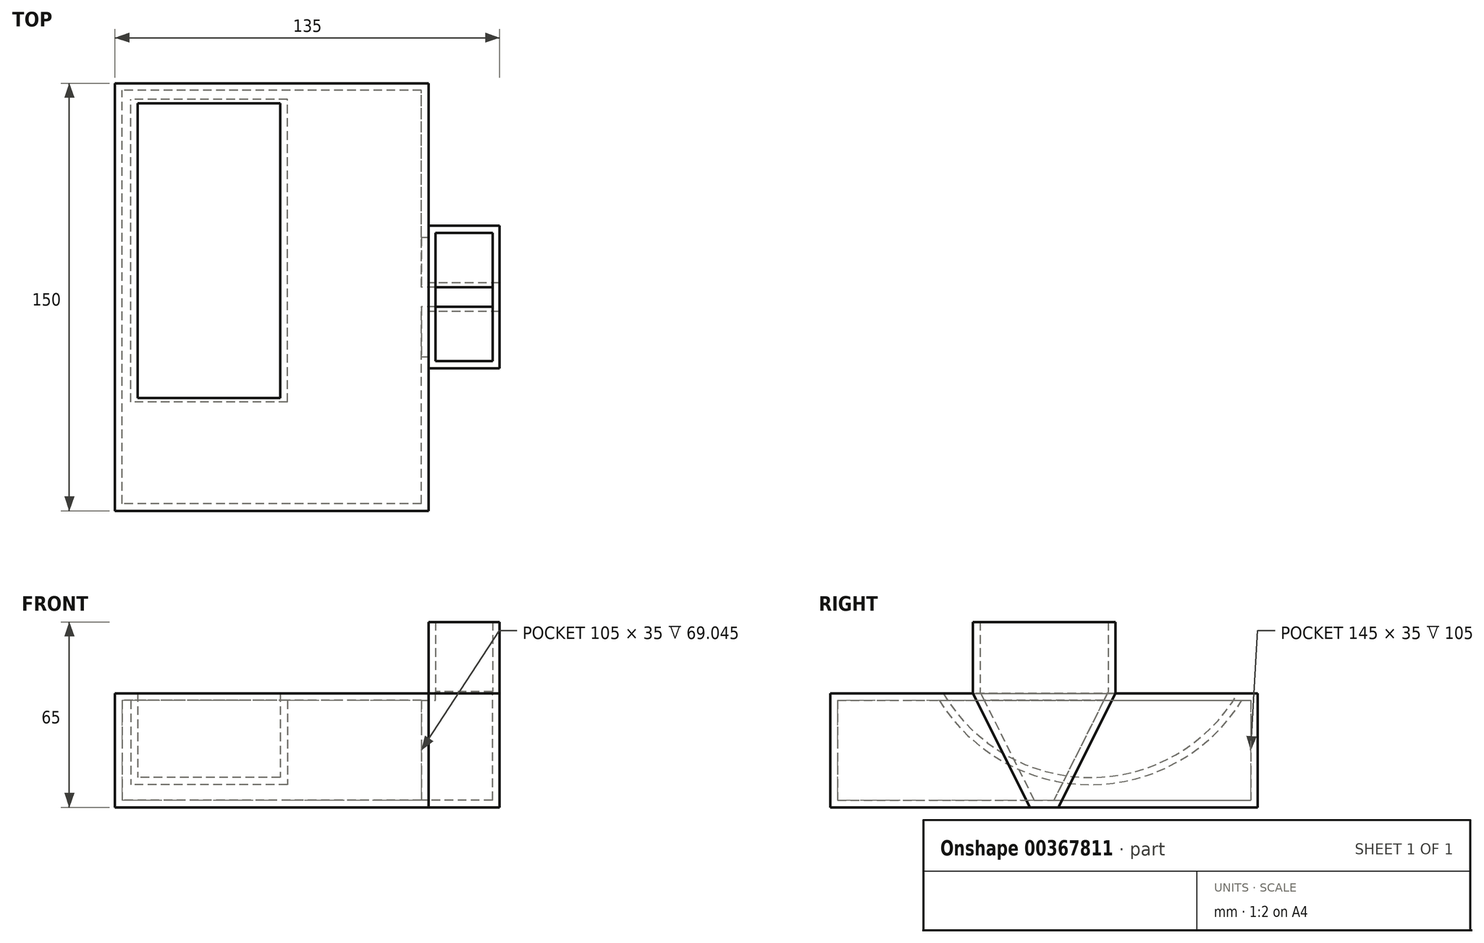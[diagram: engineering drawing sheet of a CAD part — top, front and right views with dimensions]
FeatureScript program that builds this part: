
annotation { "Feature Type Name" : "Feature", "Feature Type Description" : "" }
export const myFeature = defineFeature(function(context is Context, id is Id, definition is map)
    precondition{}
    {
        {
            var Q0;
            Q0=qCreatedBy(makeId("Top.planeOp"),FACE);
            var sketch = newSketch(context, id + "F0", { "sketchPlane" : qUnion([Q0])});
            skLineSegment(sketch, "E0.bottom", {"start": v(55, -75) * mm, "end": v(-55, -75) * mm});
            skLineSegment(sketch, "E0.top", {"start": v(55, 75) * mm, "end": v(-55, 75) * mm});
            skLineSegment(sketch, "E0.left", {"start": v(55, -75) * mm, "end": v(55, 75) * mm});
            skLineSegment(sketch, "E0.right", {"start": v(-55, -75) * mm, "end": v(-55, 75) * mm});
            skPoint(sketch, "E0.middle", {"position": v(0, 0) * mm});
            skSolve(sketch);
        }
        {
            var Q0;
            Q0=makeQuery(id+"F0.imprint","IMPRINT",FACE,{"disambiguationData":[TD([[makeQuery(id+"F0.imprint","IMPRINT",EDGE,{"derivedFrom":sQuery(id+"F0.wireOp",EDGE,"E0.bottom")}),-1.0]])]});
            extrude(context, id + "F1", {"entities" : qUnion([Q0]), "depth" : 40 * mm});
        }
        {
            var Q0;
            Q0=qCreatedBy(makeId("Right.planeOp"),FACE);
            cPlane(context, id + "F2", {"entities" : qUnion([Q0]), "cplaneType" : CPlaneType.OFFSET, "offset" : 47 * mm, "oppositeDirection" : true, "width" : 150 * mm, "height" : 150 * mm});
        }
        {
            var Q0;
            Q0=qCreatedBy(id+"F2.planeOp",FACE);
            var sketch = newSketch(context, id + "F3", { "sketchPlane" : qUnion([Q0])});
            skCircle(sketch, "E1", {"center": v(16.3, 70.46) * mm, "radius": 60 * mm});
            skSolve(sketch);
        }
        {
            var Q0;
            Q0=makeQuery(id+"F3.imprint","IMPRINT",FACE,{"disambiguationData":[TD([[makeQuery(id+"F3.imprint","IMPRINT",EDGE,{"derivedFrom":sQuery(id+"F3.wireOp",EDGE,"E1")}),1.0]])]});
            var Q1;
            Q1=sQuery(id+"F3.wireOp",EDGE,"E1");
            extrude(context, id + "F4", {"entities" : qUnion([Q0]), "operationType" : NewBodyOperationType.REMOVE, "surfaceEntities" : qUnion([Q1]), "depth" : 50 * mm});
        }
        {
            var Q0;
            Q0=makeQuery(id+"F1.opExtrude","SWEPT_FACE",FACE,{"disambiguationData":[OSD([sQuery(id+"F0.wireOp",EDGE,"E0.left")])]});
            var sketch = newSketch(context, id + "F5", { "sketchPlane" : qUnion([Q0])});
            skLineSegment(sketch, "E2", {"start": v(5, 0) * mm, "end": v(-5, 0) * mm});
            skLineSegment(sketch, "E3", {"start": v(-5, 0) * mm, "end": v(-25, 40) * mm});
            skLineSegment(sketch, "E4", {"start": v(-25, 40) * mm, "end": v(25, 40) * mm});
            skLineSegment(sketch, "E5", {"start": v(25, 40) * mm, "end": v(5, 0) * mm});
            skLineSegment(sketch, "E6", {"start": v(0, 0) * mm, "end": v(0, 40) * mm, "construction": true});
            skSolve(sketch);
        }
        {
            var Q0;
            Q0 = qSketchRegion(id + "F5", true);
            extrude(context, id + "F6", {"entities" : qUnion([Q0]), "operationType" : NewBodyOperationType.ADD, "depth" : 25 * mm});
        }
        {
            var Q0;
            Q0=makeQuery(id+"F6.boolean.opBoolean","MERGE",FACE,{"derivedFrom":[makeQuery(id+"F1.opExtrude","CAP_FACE",FACE,{"disambiguationData":[OSD([sQuery(id+"F0.wireOp",EDGE,"E0.bottom"),sQuery(id+"F0.wireOp",EDGE,"E0.top"),sQuery(id+"F0.wireOp",EDGE,"E0.left"),sQuery(id+"F0.wireOp",EDGE,"E0.right")])],"isStart":false}),makeQuery(id+"F6.opExtrude","SWEPT_FACE",FACE,{"disambiguationData":[OSD([sQuery(id+"F5.wireOp",EDGE,"E4")])]})]});
            var sketch = newSketch(context, id + "F7", { "sketchPlane" : qUnion([Q0])});
            skLineSegment(sketch, "E7.0", {"start": v(80, 25) * mm, "end": v(55, 25) * mm});
            skLineSegment(sketch, "E7.1", {"start": v(80, -25) * mm, "end": v(80, 25) * mm});
            skLineSegment(sketch, "E7.2", {"start": v(80, -25) * mm, "end": v(55, -25) * mm});
            skLineSegment(sketch, "E8", {"start": v(55, 25) * mm, "end": v(55, -25) * mm});
            skSolve(sketch);
        }
        {
            var Q0;
            Q0 = qSketchRegion(id + "F7", true);
            extrude(context, id + "F8", {"entities" : qUnion([Q0]), "operationType" : NewBodyOperationType.ADD, "depth" : 25 * mm});
        }
        {
            var Q0;
            Q0=makeQuery(id+"F8.opExtrude","CAP_FACE",FACE,{"disambiguationData":[OSD([sQuery(id+"F7.wireOp",EDGE,"E7.0"),sQuery(id+"F7.wireOp",EDGE,"E7.1"),sQuery(id+"F7.wireOp",EDGE,"E7.2"),sQuery(id+"F7.wireOp",EDGE,"E8")])],"isStart":false});
            shell(context, id + "F9", {"entities" : qUnion([Q0]), "thickness" : 2.5 * mm});
        }
    });
